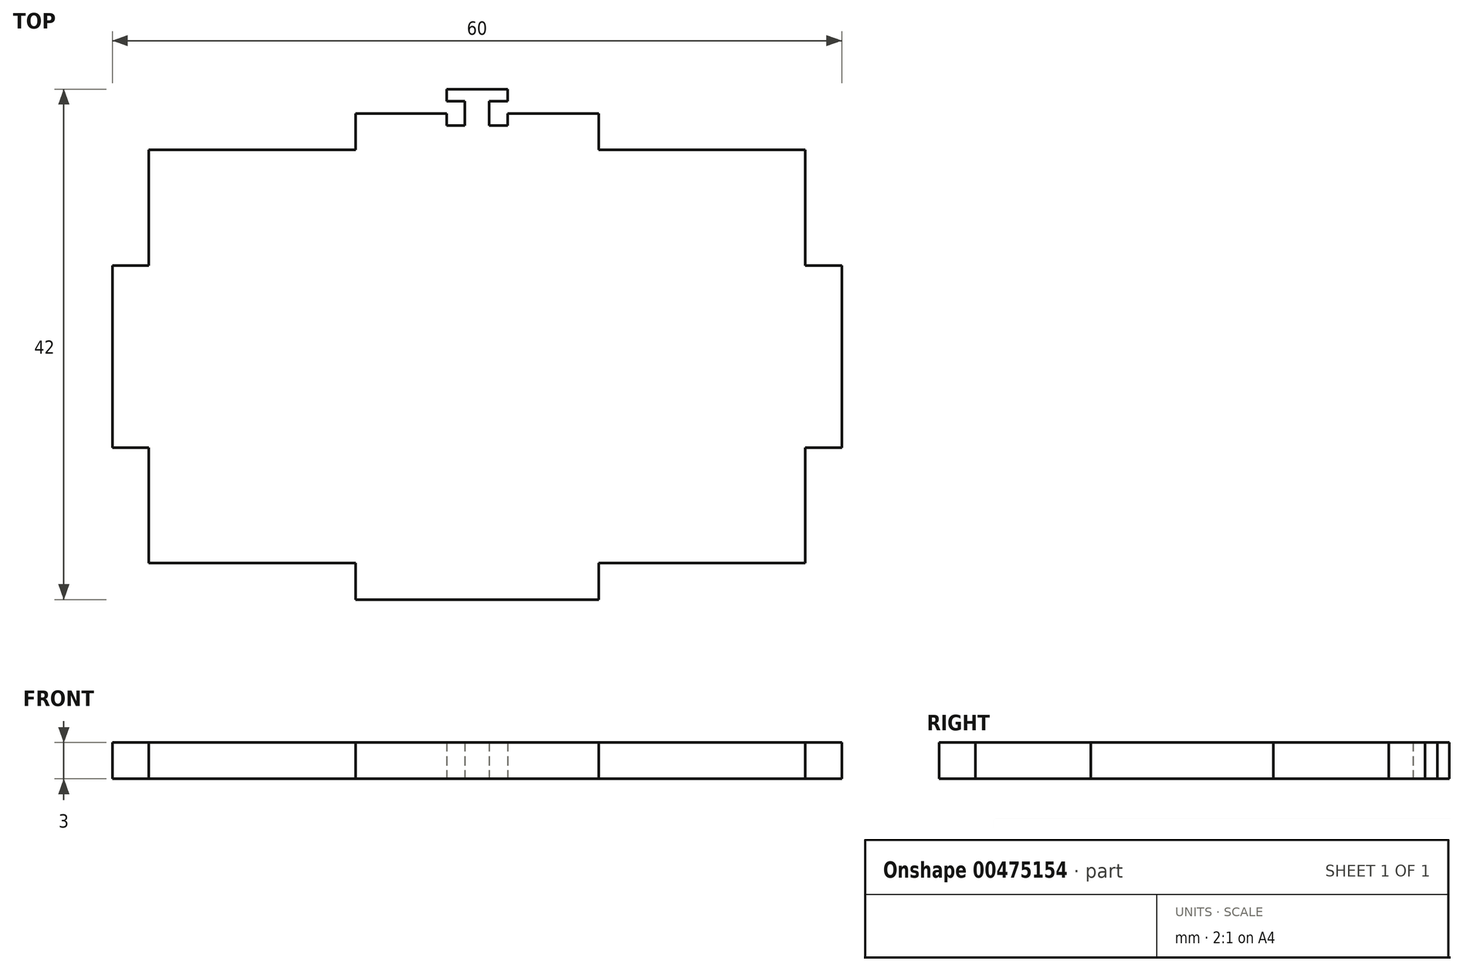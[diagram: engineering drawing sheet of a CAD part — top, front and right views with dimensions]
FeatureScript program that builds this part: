
annotation { "Feature Type Name" : "Feature", "Feature Type Description" : "" }
export const myFeature = defineFeature(function(context is Context, id is Id, definition is map)
    precondition{}
    {
        {
            var Q0;
            Q0=qCreatedBy(makeId("Top.planeOp"),FACE);
            var sketch = newSketch(context, id + "F0", { "sketchPlane" : qUnion([Q0])});
            skLineSegment(sketch, "E0.bottom", {"start": v(10, 20) * mm, "end": v(2.5, 20) * mm});
            skLineSegment(sketch, "E0.top", {"start": v(10, -20) * mm, "end": v(-10, -20) * mm});
            skLineSegment(sketch, "E0.right", {"start": v(-30, 7.5) * mm, "end": v(-30, -7.5) * mm});
            skPoint(sketch, "E0.middle", {"position": v(0, 0) * mm});
            skLineSegment(sketch, "E1", {"start": v(-27, 17) * mm, "end": v(-27, 7.5) * mm});
            skLineSegment(sketch, "E2", {"start": v(-27, 7.5) * mm, "end": v(-30, 7.5) * mm});
            skPoint(sketch, "E3.orphan", {"position": v(-30, 20) * mm});
            skLineSegment(sketch, "E4", {"start": v(-30, -7.5) * mm, "end": v(-27, -7.5) * mm});
            skLineSegment(sketch, "E5", {"start": v(-27, -7.5) * mm, "end": v(-27, -17) * mm});
            skPoint(sketch, "E6.orphan", {"position": v(-30, -20) * mm});
            skLineSegment(sketch, "E7", {"start": v(27, 17) * mm, "end": v(27, 7.5) * mm});
            skLineSegment(sketch, "E8", {"start": v(27, 7.5) * mm, "end": v(30, 7.5) * mm});
            skLineSegment(sketch, "E9", {"start": v(27, -17) * mm, "end": v(27, -7.5) * mm});
            skLineSegment(sketch, "E10", {"start": v(27, -7.5) * mm, "end": v(30, -7.5) * mm});
            skPoint(sketch, "E11.orphan", {"position": v(30, -20) * mm});
            skPoint(sketch, "E12.orphan", {"position": v(30, 20) * mm});
            skLineSegment(sketch, "E13", {"start": v(30, -7.5) * mm, "end": v(30, 7.5) * mm});
            skLineSegment(sketch, "E14", {"start": v(-27, -17) * mm, "end": v(-10, -17) * mm});
            skLineSegment(sketch, "E15", {"start": v(-10, -17) * mm, "end": v(-10, -20) * mm});
            skLineSegment(sketch, "E16", {"start": v(27, -17) * mm, "end": v(10, -17) * mm});
            skLineSegment(sketch, "E17", {"start": v(10, -17) * mm, "end": v(10, -20) * mm});
            skLineSegment(sketch, "E18", {"start": v(-10, -20) * mm, "end": v(10, -20) * mm});
            skPoint(sketch, "E19.orphan", {"position": v(27, -20) * mm});
            skLineSegment(sketch, "E20", {"start": v(-27, 17) * mm, "end": v(-10, 17) * mm});
            skLineSegment(sketch, "E21", {"start": v(-10, 17) * mm, "end": v(-10, 20) * mm});
            skLineSegment(sketch, "E22", {"start": v(27, 17) * mm, "end": v(10, 17) * mm});
            skLineSegment(sketch, "E23", {"start": v(10, 17) * mm, "end": v(10, 20) * mm});
            skLineSegment(sketch, "E24", {"start": v(-10, 20) * mm, "end": v(-2.5, 20) * mm});
            skLineSegment(sketch, "E25", {"start": v(0, 20) * mm, "end": v(1, 20) * mm});
            skLineSegment(sketch, "E26.bottom", {"start": v(2.5, 22) * mm, "end": v(-2.5, 22) * mm});
            skLineSegment(sketch, "E26.top", {"start": v(2.5, 18) * mm, "end": v(-2.5, 18) * mm});
            skLineSegment(sketch, "E26.left", {"start": v(2.5, 22) * mm, "end": v(2.5, 21) * mm});
            skLineSegment(sketch, "E26.right", {"start": v(-2.5, 22) * mm, "end": v(-2.5, 21) * mm});
            skPoint(sketch, "E26.middle", {"position": v(0, 20) * mm});
            skLineSegment(sketch, "E27", {"start": v(-2.5, 20) * mm, "end": v(-2.5, 19) * mm});
            skLineSegment(sketch, "E28", {"start": v(-2.5, 19) * mm, "end": v(-2.5, 18) * mm});
            skLineSegment(sketch, "E29", {"start": v(-2.5, 21) * mm, "end": v(-1, 21) * mm});
            skLineSegment(sketch, "E30", {"start": v(-1, 21) * mm, "end": v(-1, 19) * mm});
            skLineSegment(sketch, "E31", {"start": v(-1, 19) * mm, "end": v(-2.5, 19) * mm});
            skLineSegment(sketch, "E32", {"start": v(2.5, 20) * mm, "end": v(2.5, 19) * mm});
            skLineSegment(sketch, "E33", {"start": v(2.5, 19) * mm, "end": v(2.5, 18) * mm});
            skLineSegment(sketch, "E34", {"start": v(2.5, 21) * mm, "end": v(1, 21) * mm});
            skLineSegment(sketch, "E35", {"start": v(1, 21) * mm, "end": v(1, 19) * mm});
            skLineSegment(sketch, "E36", {"start": v(1, 19) * mm, "end": v(2.5, 19) * mm});
            skLineSegment(sketch, "E37", {"start": v(0, 20) * mm, "end": v(0, 16) * mm});
            skPoint(sketch, "E37.endSnap0", {"position": v(0, 18) * mm});
            skLineSegment(sketch, "E38", {"start": v(-2.5, 18) * mm, "end": v(0, 16) * mm});
            skLineSegment(sketch, "E39", {"start": v(0, 16) * mm, "end": v(2.5, 18) * mm});
            skLineSegment(sketch, "E40.trimOffspring", {"start": v(-1, 20) * mm, "end": v(0, 20) * mm});
            skLineSegment(sketch, "E41.trimOffspring", {"start": v(-2.5, 20) * mm, "end": v(-10, 20) * mm});
            skLineSegment(sketch, "E42.trimOffspring", {"start": v(2.5, 20) * mm, "end": v(10, 20) * mm});
            skLineSegment(sketch, "E43.trimOffspring", {"start": v(2.5, 20) * mm, "end": v(2.5, 18) * mm});
            skLineSegment(sketch, "E44.trimOffspring", {"start": v(1, 20) * mm, "end": v(-1, 20) * mm});
            skLineSegment(sketch, "E45", {"start": v(-2.5, 20) * mm, "end": v(-2, 20) * mm});
            skLineSegment(sketch, "E46", {"start": v(-2, 20) * mm, "end": v(-2, 19.7) * mm});
            skLineSegment(sketch, "E47", {"start": v(-2, 19.7) * mm, "end": v(-2.5, 19.7) * mm});
            skSolve(sketch);
        }
        {
            var Q0;
            Q0=makeQuery(id+"F0.imprint","IMPRINT",FACE,{"disambiguationData":[TD([[makeQuery(id+"F0.imprint","IMPRINT",EDGE,{"derivedFrom":sQuery(id+"F0.wireOp",EDGE,"E0.right")}),1.0]])]});
            var Q1;
            {var subQ0=sQuery(id+"F0.wireOp",EDGE,"E39");Q1=makeQuery(id+"F0.imprint","IMPRINT",FACE,{"disambiguationData":[TD([[makeQuery(id+"F0.imprint","IMPRINT",EDGE,{"derivedFrom":subQ0}),1.0]])]});}
            var Q2;
            {var subQ0=sQuery(id+"F0.wireOp",EDGE,"E38");Q2=makeQuery(id+"F0.imprint","IMPRINT",FACE,{"disambiguationData":[TD([[makeQuery(id+"F0.imprint","IMPRINT",EDGE,{"derivedFrom":subQ0}),1.0]])]});}
            var Q3;
            {var subQ5=sQuery(id+"F0.wireOp",EDGE,"E31");Q3=makeQuery(id+"F0.imprint","IMPRINT",FACE,{"disambiguationData":[TD([[makeQuery(id+"F0.imprint","IMPRINT",EDGE,{"derivedFrom":subQ5}),1.0]])]});}
            var Q4;
            {var subQ5=sQuery(id+"F0.wireOp",EDGE,"E36");Q4=makeQuery(id+"F0.imprint","IMPRINT",FACE,{"disambiguationData":[TD([[makeQuery(id+"F0.imprint","IMPRINT",EDGE,{"derivedFrom":subQ5}),-1.0]])]});}
            var Q5;
            Q5=makeQuery(id+"F0.imprint","IMPRINT",FACE,{"disambiguationData":[TD([[makeQuery(id+"F0.imprint","IMPRINT",EDGE,{"derivedFrom":sQuery(id+"F0.wireOp",EDGE,"E26.bottom")}),1.0]])]});
            extrude(context, id + "F1", {"entities" : qUnion([Q0, Q1, Q2, Q3, Q4, Q5]), "depth" : 3 * mm});
        }
    });
